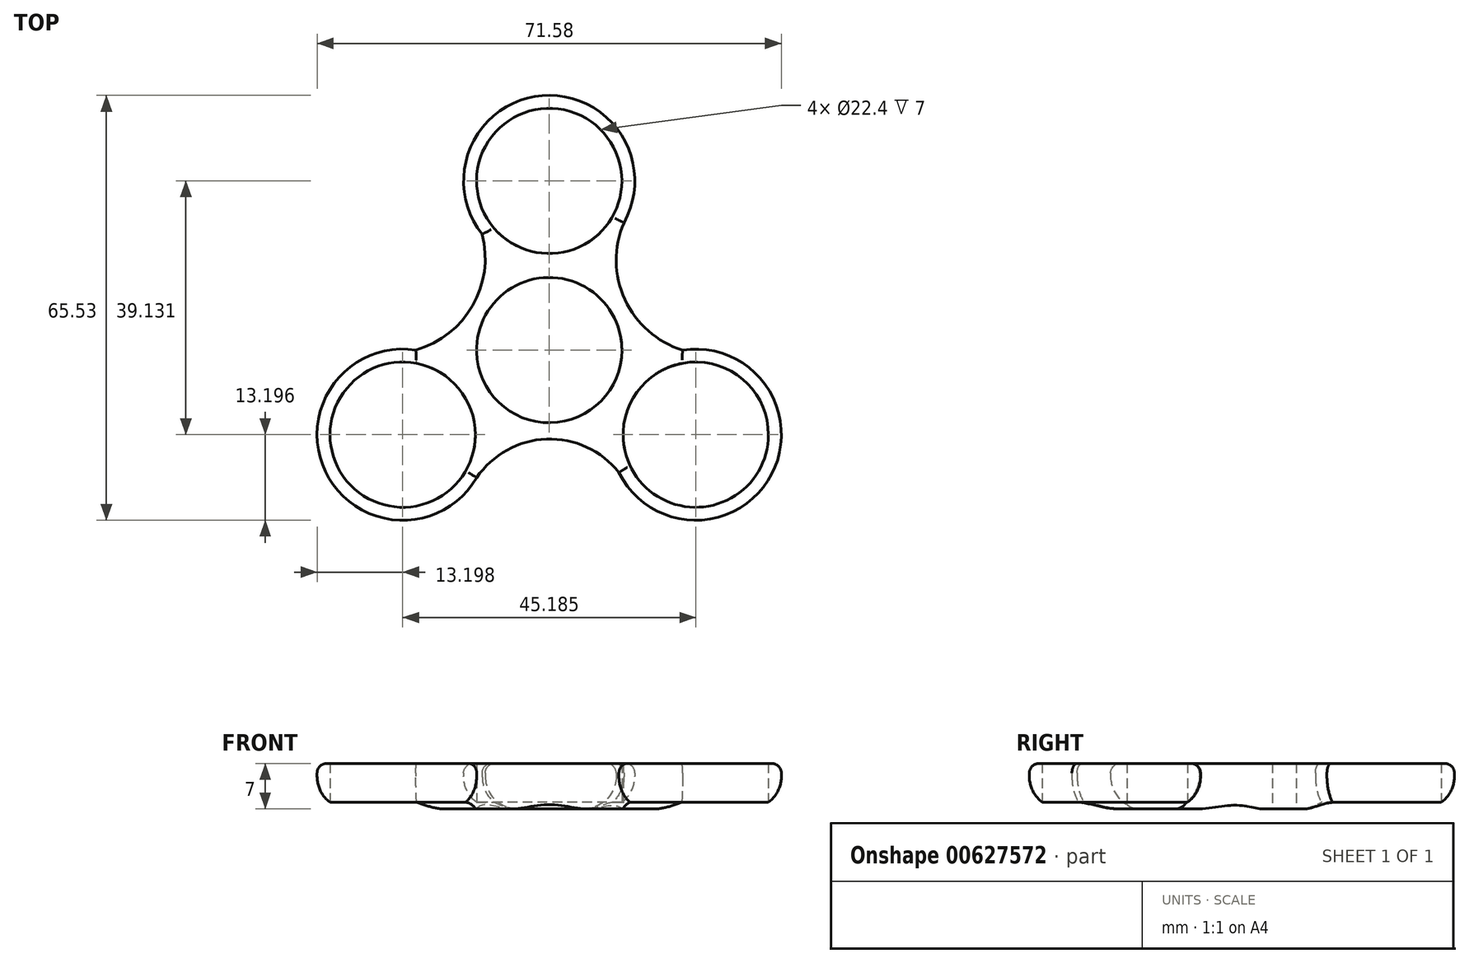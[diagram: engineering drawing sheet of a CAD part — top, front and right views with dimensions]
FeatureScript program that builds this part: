
annotation { "Feature Type Name" : "Feature", "Feature Type Description" : "" }
export const myFeature = defineFeature(function(context is Context, id is Id, definition is map)
    precondition{}
    {
        {
            var Q0;
            Q0=qCreatedBy(makeId("Top.planeOp"),FACE);
            var sketch = newSketch(context, id + "F0", { "sketchPlane" : qUnion([Q0])});
            skCircle(sketch, "E0", {"center": v(0, 0) * mm, "radius": 11.2 * mm});
            skCircle(sketch, "E1", {"center": v(0, 26.09) * mm, "radius": 11.2 * mm});
            skCircle(sketch, "E2.1.0", {"center": v(-22.6, -13.04) * mm, "radius": 11.2 * mm});
            skArc(sketch, "E2.1.1", {"start": v(-20.57, 0) * mm, "mid": v(-34.5, -18.73) * mm, "end": v(-11.18, -19.68) * mm});
            skCircle(sketch, "E2.2.0", {"center": v(22.6, -13.04) * mm, "radius": 11.2 * mm});
            skArc(sketch, "E2.2.1", {"start": v(10.75, -18.87) * mm, "mid": v(34.3, -19.13) * mm, "end": v(20.57, 0) * mm});
            skArc(sketch, "E3", {"start": v(-20.57, 0) * mm, "mid": v(-11.82, 6.86) * mm, "end": v(-10.33, 17.87) * mm});
            skArc(sketch, "E4", {"start": v(10.75, -18.87) * mm, "mid": v(-0.42, -13.72) * mm, "end": v(-11.18, -19.68) * mm});
            skArc(sketch, "E5", {"start": v(11.52, 19.64) * mm, "mid": v(11.66, 7.8) * mm, "end": v(20.57, 0) * mm});
            skArc(sketch, "E6.trimOffspring", {"start": v(11.52, 19.64) * mm, "mid": v(-1.06, 39.24) * mm, "end": v(-10.33, 17.87) * mm});
            skSolve(sketch);
        }
        {
            var Q0;
            Q0=makeQuery(id+"F0.imprint","IMPRINT",FACE,{"disambiguationData":[TD([[makeQuery(id+"F0.imprint","IMPRINT",EDGE,{"derivedFrom":sQuery(id+"F0.wireOp",EDGE,"E0")}),-1.0]])]});
            extrude(context, id + "F1", {"entities" : qUnion([Q0]), "depth" : 7 * mm, "offsetDistance" : 25 * mm});
        }
        {
            var Q0;
            Q0=makeQuery(id+"F1.opExtrude","CAP_EDGE",EDGE,{"disambiguationData":[OSD([sQuery(id+"F0.wireOp",EDGE,"E4")])],"isStart":false});
            var Q1;
            Q1=makeQuery(id+"F1.opExtrude","CAP_EDGE",EDGE,{"disambiguationData":[OSD([sQuery(id+"F0.wireOp",EDGE,"E2.1.1")])],"isStart":false});
            var Q2;
            Q2=makeQuery(id+"F1.opExtrude","CAP_EDGE",EDGE,{"disambiguationData":[OSD([sQuery(id+"F0.wireOp",EDGE,"E3")])],"isStart":false});
            var Q3;
            Q3=makeQuery(id+"F1.opExtrude","CAP_EDGE",EDGE,{"disambiguationData":[OSD([sQuery(id+"F0.wireOp",EDGE,"E6.trimOffspring")])],"isStart":false});
            var Q4;
            Q4=makeQuery(id+"F1.opExtrude","CAP_EDGE",EDGE,{"disambiguationData":[OSD([sQuery(id+"F0.wireOp",EDGE,"E2.2.1")])],"isStart":false});
            var Q5;
            Q5=makeQuery(id+"F1.opExtrude","CAP_EDGE",EDGE,{"disambiguationData":[OSD([sQuery(id+"F0.wireOp",EDGE,"E5")])],"isStart":false});
            fillet(context, id + "F2", {"entities" : qUnion([Q0, Q1, Q2, Q3, Q4, Q5]), "radius" : 1.5 * mm, "tangentPropagation" : true, "allowEdgeOverflow" : false});
        }
        {
            var Q0;
            Q0=makeQuery(id+"F1.opExtrude","CAP_EDGE",EDGE,{"disambiguationData":[OSD([sQuery(id+"F0.wireOp",EDGE,"E2.1.1")])],"isStart":true});
            var Q1;
            Q1=makeQuery(id+"F1.opExtrude","CAP_EDGE",EDGE,{"disambiguationData":[OSD([sQuery(id+"F0.wireOp",EDGE,"E4")])],"isStart":true});
            var Q2;
            Q2=makeQuery(id+"F1.opExtrude","CAP_EDGE",EDGE,{"disambiguationData":[OSD([sQuery(id+"F0.wireOp",EDGE,"E2.2.1")])],"isStart":true});
            var Q3;
            Q3=makeQuery(id+"F1.opExtrude","CAP_EDGE",EDGE,{"disambiguationData":[OSD([sQuery(id+"F0.wireOp",EDGE,"E5")])],"isStart":true});
            var Q4;
            Q4=makeQuery(id+"F1.opExtrude","CAP_EDGE",EDGE,{"disambiguationData":[OSD([sQuery(id+"F0.wireOp",EDGE,"E6.trimOffspring")])],"isStart":true});
            var Q5;
            Q5=makeQuery(id+"F1.opExtrude","CAP_EDGE",EDGE,{"disambiguationData":[OSD([sQuery(id+"F0.wireOp",EDGE,"E3")])],"isStart":true});
            fillet(context, id + "F3", {"entities" : qUnion([Q0, Q1, Q2, Q3, Q4, Q5]), "radius" : 5 * mm, "tangentPropagation" : true, "allowEdgeOverflow" : false});
        }
    });
